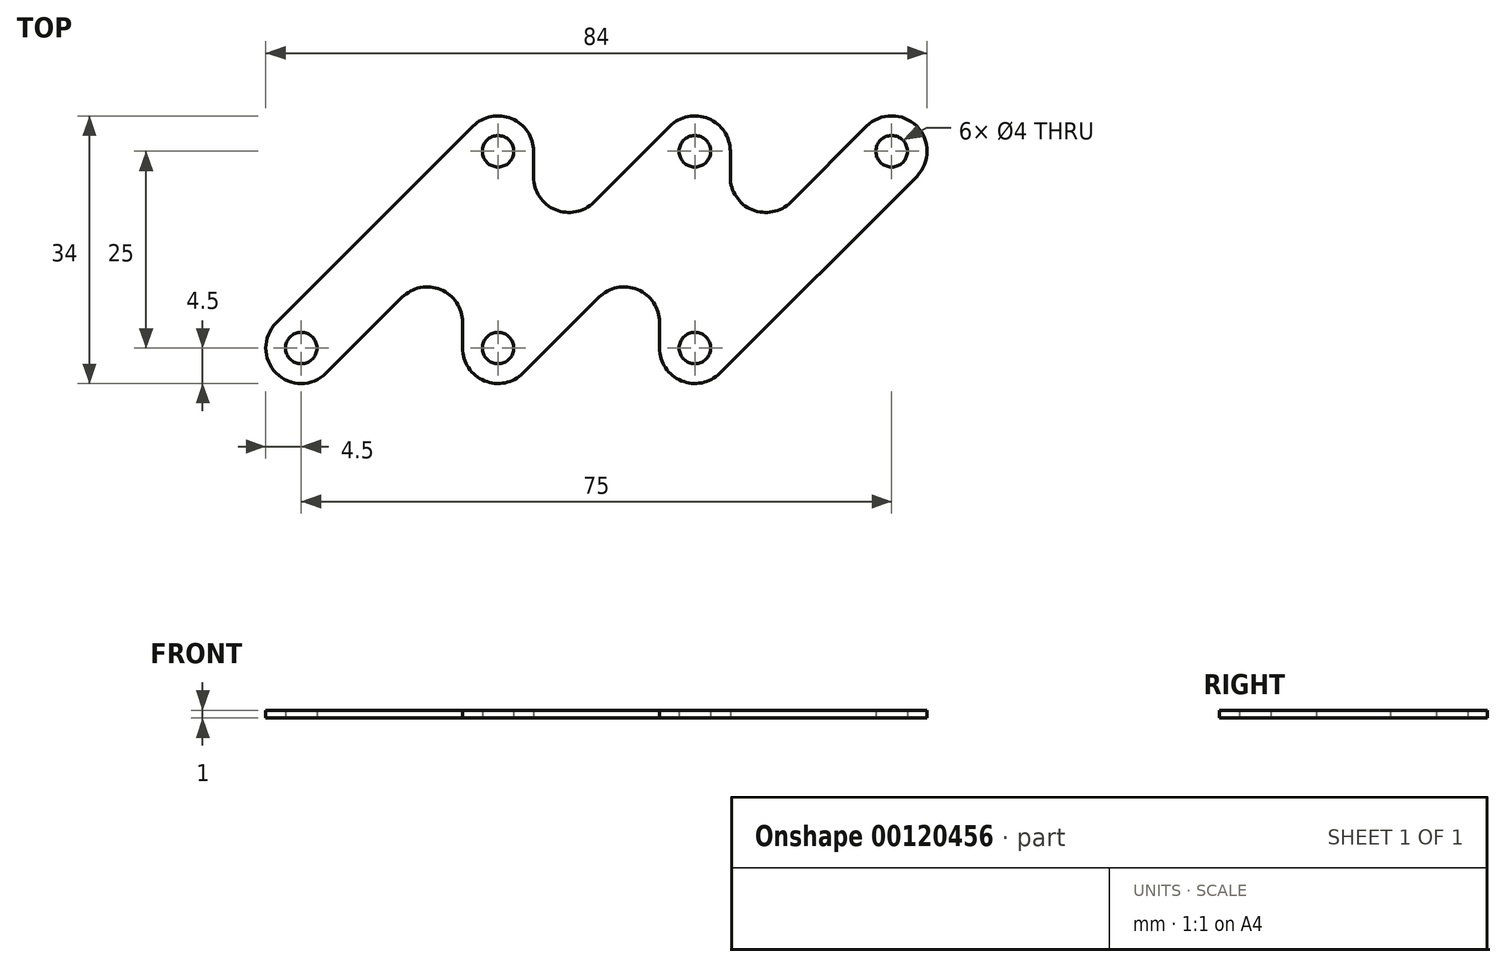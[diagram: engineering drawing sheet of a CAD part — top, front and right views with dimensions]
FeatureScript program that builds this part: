
annotation { "Feature Type Name" : "Feature", "Feature Type Description" : "" }
export const myFeature = defineFeature(function(context is Context, id is Id, definition is map)
    precondition{}
    {
        {
            var Q0;
            Q0=qCreatedBy(makeId("Top.planeOp"),FACE);
            var sketch = newSketch(context, id + "F0", { "sketchPlane" : qUnion([Q0])});
            skPoint(sketch, "E0", {"position": v(0, 0) * mm});
            skPoint(sketch, "E1", {"position": v(25, 25) * mm});
            skPoint(sketch, "E2.1.0.0", {"position": v(25, 0) * mm});
            skPoint(sketch, "E2.1.0.1", {"position": v(50, 25) * mm});
            skPoint(sketch, "E2.2.0.0", {"position": v(50, 0) * mm});
            skPoint(sketch, "E2.2.0.1", {"position": v(75, 25) * mm});
            skLineSegment(sketch, "E2.direction1", {"start": v(0, 0) * mm, "end": v(25, 0) * mm, "construction": true});
            skCircle(sketch, "E3", {"center": v(0, 0) * mm, "radius": 2 * mm});
            skCircle(sketch, "E4", {"center": v(25, 25) * mm, "radius": 2 * mm});
            skCircle(sketch, "E5", {"center": v(25, 0) * mm, "radius": 2 * mm});
            skCircle(sketch, "E6", {"center": v(50, 25) * mm, "radius": 2 * mm});
            skCircle(sketch, "E7", {"center": v(50, 0) * mm, "radius": 2 * mm});
            skCircle(sketch, "E8", {"center": v(75, 25) * mm, "radius": 2 * mm});
            skArc(sketch, "E9", {"start": v(-3.18, 3.18) * mm, "mid": v(-3.18, -3.18) * mm, "end": v(3.18, -3.18) * mm});
            skCircle(sketch, "E10", {"center": v(25, 25) * mm, "radius": 4.5 * mm});
            skCircle(sketch, "E11", {"center": v(25, 0) * mm, "radius": 4.5 * mm});
            skCircle(sketch, "E12", {"center": v(50, 25) * mm, "radius": 4.5 * mm});
            skCircle(sketch, "E13", {"center": v(50, 0) * mm, "radius": 4.5 * mm});
            skCircle(sketch, "E14", {"center": v(75, 25) * mm, "radius": 4.5 * mm});
            skLineSegment(sketch, "E15", {"start": v(-3.18, 3.18) * mm, "end": v(21.82, 28.18) * mm});
            skLineSegment(sketch, "E16", {"start": v(3.18, -3.18) * mm, "end": v(20.5, 14.14) * mm});
            skLineSegment(sketch, "E17", {"start": v(20.5, 14.14) * mm, "end": v(20.5, 0) * mm});
            skLineSegment(sketch, "E18", {"start": v(29.5, 10.86) * mm, "end": v(29.5, 25) * mm});
            skLineSegment(sketch, "E19", {"start": v(46.82, 28.18) * mm, "end": v(29.5, 10.86) * mm});
            skLineSegment(sketch, "E20", {"start": v(45.5, 14.14) * mm, "end": v(28.18, -3.18) * mm});
            skLineSegment(sketch, "E21", {"start": v(45.5, 14.14) * mm, "end": v(45.5, 0) * mm});
            skLineSegment(sketch, "E22", {"start": v(54.5, 25) * mm, "end": v(54.5, 10.86) * mm});
            skLineSegment(sketch, "E23", {"start": v(54.5, 10.86) * mm, "end": v(71.82, 28.18) * mm});
            skLineSegment(sketch, "E24", {"start": v(53.18, -3.18) * mm, "end": v(78.18, 21.82) * mm});
            skPoint(sketch, "E25.orphan", {"position": v(29.5, 0) * mm});
            skPoint(sketch, "E26.orphan", {"position": v(54.5, 0) * mm});
            skSolve(sketch);
        }
        {
            var Q0;
            Q0=makeQuery(id+"F0.imprint","IMPRINT",FACE,{"disambiguationData":[TD([[makeQuery(id+"F0.imprint","IMPRINT",EDGE,{"derivedFrom":sQuery(id+"F0.wireOp",EDGE,"E3")}),-1.0]])]});
            var Q1;
            Q1=makeQuery(id+"F0.imprint","IMPRINT",FACE,{"disambiguationData":[TD([[makeQuery(id+"F0.imprint","IMPRINT",EDGE,{"derivedFrom":sQuery(id+"F0.wireOp",EDGE,"E4")}),-1.0]])]});
            var Q2;
            Q2=makeQuery(id+"F0.imprint","IMPRINT",FACE,{"disambiguationData":[TD([[makeQuery(id+"F0.imprint","IMPRINT",EDGE,{"derivedFrom":sQuery(id+"F0.wireOp",EDGE,"E5")}),-1.0]])]});
            var Q3;
            Q3=makeQuery(id+"F0.imprint","IMPRINT",FACE,{"disambiguationData":[TD([[makeQuery(id+"F0.imprint","IMPRINT",EDGE,{"derivedFrom":sQuery(id+"F0.wireOp",EDGE,"E7")}),-1.0]])]});
            var Q4;
            Q4=makeQuery(id+"F0.imprint","IMPRINT",FACE,{"disambiguationData":[TD([[makeQuery(id+"F0.imprint","IMPRINT",EDGE,{"derivedFrom":sQuery(id+"F0.wireOp",EDGE,"E6")}),-1.0]])]});
            var Q5;
            Q5=makeQuery(id+"F0.imprint","IMPRINT",FACE,{"disambiguationData":[TD([[makeQuery(id+"F0.imprint","IMPRINT",EDGE,{"derivedFrom":sQuery(id+"F0.wireOp",EDGE,"E8")}),-1.0]])]});
            extrude(context, id + "F1", {"entities" : qUnion([Q0, Q1, Q2, Q3, Q4, Q5]), "depth" : 1 * mm});
        }
        {
            var Q0;
            Q0=makeQuery(id+"F1.opExtrude","SWEPT_EDGE",EDGE,{"disambiguationData":[OSD([sQuery(id+"F0.wireOp",EDGE,"E16"),sQuery(id+"F0.wireOp",EDGE,"E17")])]});
            var Q1;
            Q1=makeQuery(id+"F1.opExtrude","SWEPT_EDGE",EDGE,{"disambiguationData":[OSD([sQuery(id+"F0.wireOp",EDGE,"E20"),sQuery(id+"F0.wireOp",EDGE,"E21")])]});
            var Q2;
            Q2=makeQuery(id+"F1.opExtrude","SWEPT_EDGE",EDGE,{"disambiguationData":[OSD([sQuery(id+"F0.wireOp",EDGE,"E18"),sQuery(id+"F0.wireOp",EDGE,"E19")])]});
            var Q3;
            Q3=makeQuery(id+"F1.opExtrude","SWEPT_EDGE",EDGE,{"disambiguationData":[OSD([sQuery(id+"F0.wireOp",EDGE,"E22"),sQuery(id+"F0.wireOp",EDGE,"E23")])]});
            fillet(context, id + "F2", {"entities" : qUnion([Q0, Q1, Q2, Q3]), "radius" : 4.5 * mm, "tangentPropagation" : true, "allowEdgeOverflow" : false});
        }
    });
